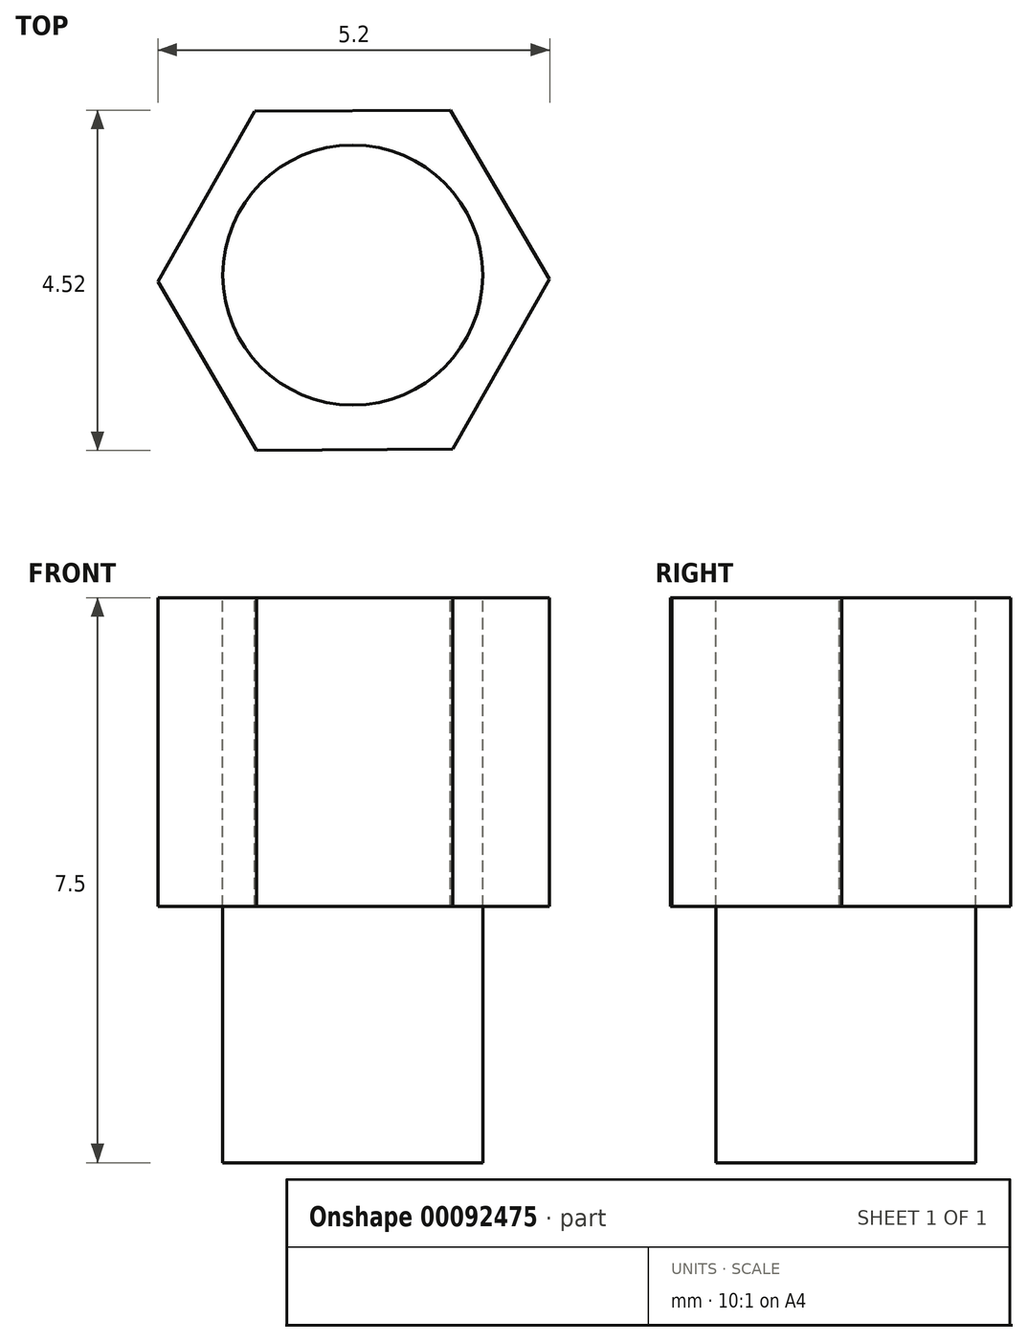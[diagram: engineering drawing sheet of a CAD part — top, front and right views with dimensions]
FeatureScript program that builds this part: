
annotation { "Feature Type Name" : "Feature", "Feature Type Description" : "" }
export const myFeature = defineFeature(function(context is Context, id is Id, definition is map)
    precondition{}
    {
        {
            var Q0;
            Q0=qCreatedBy(makeId("Top.planeOp"),FACE);
            var sketch = newSketch(context, id + "F0", { "sketchPlane" : qUnion([Q0])});
            skCircle(sketch, "E0", {"center": v(-0.17, -0.18) * mm, "radius": 1.73 * mm});
            skCircle(sketch, "E1.cCircle", {"center": v(-0.16, -0.25) * mm, "radius": 2.25 * mm, "construction": true});
            skLineSegment(sketch, "E1.0", {"start": v(-2.76, -0.27) * mm, "end": v(-1.48, 2) * mm});
            skLineSegment(sketch, "E1.1", {"start": v(-1.48, 2) * mm, "end": v(1.12, 2) * mm});
            skLineSegment(sketch, "E1.2", {"start": v(1.12, 2) * mm, "end": v(2.44, -0.23) * mm});
            skLineSegment(sketch, "E1.3", {"start": v(2.44, -0.23) * mm, "end": v(1.15, -2.5) * mm});
            skLineSegment(sketch, "E1.4", {"start": v(1.15, -2.5) * mm, "end": v(-1.45, -2.5) * mm});
            skLineSegment(sketch, "E1.5", {"start": v(-1.45, -2.5) * mm, "end": v(-2.76, -0.27) * mm});
            skPoint(sketch, "E1.0.midPoint", {"position": v(-2.12, 0.86) * mm});
            skSolve(sketch);
        }
        {
            var Q0;
            Q0=makeQuery(id+"F0.imprint","IMPRINT",FACE,{"disambiguationData":[TD([[makeQuery(id+"F0.imprint","IMPRINT",EDGE,{"derivedFrom":sQuery(id+"F0.wireOp",EDGE,"E0")}),-1.0]])]});
            extrude(context, id + "F1", {"entities" : qUnion([Q0]), "oppositeDirection" : true, "depth" : 4.1 * mm});
        }
        {
            var Q0;
            Q0=makeQuery(id+"F0.imprint","IMPRINT",FACE,{"disambiguationData":[TD([[makeQuery(id+"F0.imprint","IMPRINT",EDGE,{"derivedFrom":sQuery(id+"F0.wireOp",EDGE,"E0")}),1.0]])]});
            extrude(context, id + "F2", {"entities" : qUnion([Q0]), "oppositeDirection" : true, "depth" : 7.5 * mm});
        }
    });
